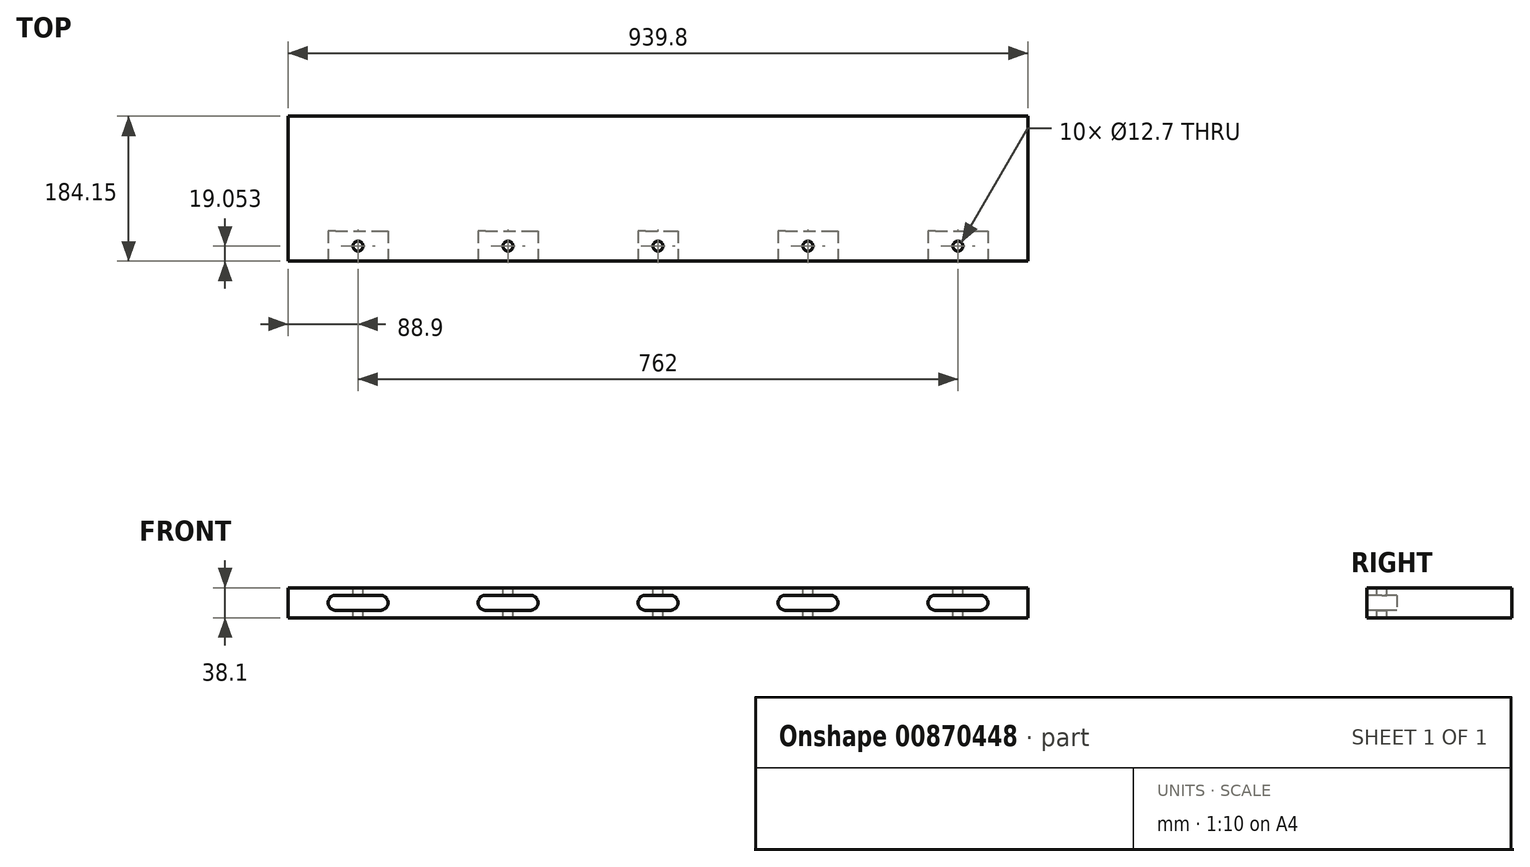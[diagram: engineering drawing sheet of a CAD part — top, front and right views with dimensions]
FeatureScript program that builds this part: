
annotation { "Feature Type Name" : "Feature", "Feature Type Description" : "" }
export const myFeature = defineFeature(function(context is Context, id is Id, definition is map)
    precondition{}
    {
        {
            var Q0;
            Q0=qCreatedBy(makeId("Right.planeOp"),FACE);
            var sketch = newSketch(context, id + "F0", { "sketchPlane" : qUnion([Q0])});
            skLineSegment(sketch, "E0.bottom", {"start": v(93.88, 19.05) * mm, "end": v(-90.27, 19.05) * mm});
            skLineSegment(sketch, "E0.top", {"start": v(93.88, -19.05) * mm, "end": v(-90.27, -19.05) * mm});
            skLineSegment(sketch, "E0.left", {"start": v(93.88, 19.05) * mm, "end": v(93.88, -19.05) * mm});
            skLineSegment(sketch, "E0.right", {"start": v(-90.27, 19.05) * mm, "end": v(-90.27, -19.05) * mm});
            skPoint(sketch, "E0.middle", {"position": v(1.8, 0) * mm});
            skSolve(sketch);
        }
        {
            var Q0;
            Q0=makeQuery(id+"F0.imprint","IMPRINT",FACE,{"disambiguationData":[TD([[makeQuery(id+"F0.imprint","IMPRINT",EDGE,{"derivedFrom":sQuery(id+"F0.wireOp",EDGE,"E0.bottom")}),1.0]])]});
            extrude(context, id + "F1", {"entities" : qUnion([Q0]), "depth" : 939.8 * mm, "offsetDistance" : 25.4 * mm});
        }
        {
            var Q0;
            Q0=makeQuery(id+"F1.opExtrude","SWEPT_FACE",FACE,{"disambiguationData":[OSD([sQuery(id+"F0.wireOp",EDGE,"E0.right")])]});
            var sketch = newSketch(context, id + "F2", { "sketchPlane" : qUnion([Q0])});
            skLineSegment(sketch, "E1.bottom", {"start": v(60.33, 9.53) * mm, "end": v(117.47, 9.53) * mm});
            skLineSegment(sketch, "E1.top", {"start": v(60.33, -9.52) * mm, "end": v(117.47, -9.52) * mm});
            skArc(sketch, "E2", {"start": v(60.33, 9.53) * mm, "mid": v(50.8, 0) * mm, "end": v(60.33, -9.53) * mm});
            skArc(sketch, "E3", {"start": v(117.47, 9.53) * mm, "mid": v(127, 0) * mm, "end": v(117.47, -9.53) * mm});
            skLineSegment(sketch, "E4", {"start": v(822.33, 9.53) * mm, "end": v(879.47, 9.53) * mm});
            skLineSegment(sketch, "E5", {"start": v(822.33, -9.53) * mm, "end": v(879.47, -9.53) * mm});
            skArc(sketch, "E6", {"start": v(822.33, 9.52) * mm, "mid": v(812.8, 0) * mm, "end": v(822.33, -9.52) * mm});
            skArc(sketch, "E7", {"start": v(879.47, 9.53) * mm, "mid": v(889, 0) * mm, "end": v(879.47, -9.53) * mm});
            skArc(sketch, "E8.1.0.0", {"start": v(250.83, 9.53) * mm, "mid": v(241.3, 0) * mm, "end": v(250.83, -9.53) * mm});
            skLineSegment(sketch, "E8.1.0.1", {"start": v(250.83, -9.52) * mm, "end": v(307.97, -9.52) * mm});
            skArc(sketch, "E8.1.0.2", {"start": v(307.97, 9.53) * mm, "mid": v(317.5, 0) * mm, "end": v(307.97, -9.53) * mm});
            skLineSegment(sketch, "E8.1.0.3", {"start": v(250.83, 9.53) * mm, "end": v(307.97, 9.53) * mm});
            skArc(sketch, "E8.2.0.0", {"start": v(441.33, 9.53) * mm, "mid": v(431.8, 0) * mm, "end": v(441.33, -9.53) * mm});
            skLineSegment(sketch, "E8.2.0.1", {"start": v(441.33, -9.52) * mm, "end": v(498.48, -9.52) * mm});
            skArc(sketch, "E8.2.0.2", {"start": v(498.48, 9.53) * mm, "mid": v(508, 0) * mm, "end": v(498.48, -9.53) * mm});
            skLineSegment(sketch, "E8.2.0.3", {"start": v(441.33, 9.53) * mm, "end": v(498.48, 9.53) * mm});
            skArc(sketch, "E8.3.0.0", {"start": v(631.83, 9.53) * mm, "mid": v(622.3, 0) * mm, "end": v(631.83, -9.53) * mm});
            skLineSegment(sketch, "E8.3.0.1", {"start": v(631.83, -9.52) * mm, "end": v(688.98, -9.52) * mm});
            skArc(sketch, "E8.3.0.2", {"start": v(688.98, 9.53) * mm, "mid": v(698.5, 0) * mm, "end": v(688.98, -9.53) * mm});
            skLineSegment(sketch, "E8.3.0.3", {"start": v(631.83, 9.53) * mm, "end": v(688.98, 9.53) * mm});
            skLineSegment(sketch, "E8.direction1", {"start": v(60.33, -9.53) * mm, "end": v(250.83, -9.53) * mm, "construction": true});
            skArc(sketch, "E9", {"start": v(454.03, 9.53) * mm, "mid": v(444.5, 0) * mm, "end": v(454.03, -9.53) * mm});
            skArc(sketch, "E10", {"start": v(485.78, -9.53) * mm, "mid": v(495.3, 0) * mm, "end": v(485.78, 9.53) * mm});
            skLineSegment(sketch, "E11", {"start": v(469.9, 23.51) * mm, "end": v(469.9, -33.12) * mm, "construction": true});
            skSolve(sketch);
        }
        {
            var Q0;
            Q0=makeQuery(id+"F2.imprint","IMPRINT",FACE,{"disambiguationData":[TD([[makeQuery(id+"F2.imprint","IMPRINT",EDGE,{"derivedFrom":sQuery(id+"F2.wireOp",EDGE,"E1.bottom")}),-1.0]])]});
            var Q1;
            Q1=makeQuery(id+"F2.imprint","IMPRINT",FACE,{"disambiguationData":[TD([[makeQuery(id+"F2.imprint","IMPRINT",EDGE,{"derivedFrom":sQuery(id+"F2.wireOp",EDGE,"E8.1.0.0")}),1.0]])]});
            var Q2;
            Q2=makeQuery(id+"F2.imprint","IMPRINT",FACE,{"disambiguationData":[TD([[makeQuery(id+"F2.imprint","IMPRINT",EDGE,{"derivedFrom":sQuery(id+"F2.wireOp",EDGE,"E8.3.0.0")}),1.0]])]});
            var Q3;
            Q3=makeQuery(id+"F2.imprint","IMPRINT",FACE,{"disambiguationData":[TD([[makeQuery(id+"F2.imprint","IMPRINT",EDGE,{"derivedFrom":sQuery(id+"F2.wireOp",EDGE,"E4")}),-1.0]])]});
            var Q4;
            {var subQ0=sQuery(id+"F2.wireOp",EDGE,"E9");Q4=makeQuery(id+"F2.imprint","IMPRINT",FACE,{"disambiguationData":[TD([[makeQuery(id+"F2.imprint","IMPRINT",EDGE,{"derivedFrom":subQ0}),1.0]])]});}
            extrude(context, id + "F3", {"entities" : qUnion([Q0, Q1, Q2, Q3, Q4]), "operationType" : NewBodyOperationType.REMOVE, "oppositeDirection" : true, "depth" : 38.1 * mm, "offsetDistance" : 25.4 * mm});
        }
        {
            var Q0;
            Q0=makeQuery(id+"F1.opExtrude","SWEPT_FACE",FACE,{"disambiguationData":[OSD([sQuery(id+"F0.wireOp",EDGE,"E0.bottom")])]});
            var sketch = newSketch(context, id + "F4", { "sketchPlane" : qUnion([Q0])});
            skCircle(sketch, "E12", {"center": v(88.9, -71.22) * mm, "radius": 6.35 * mm});
            skCircle(sketch, "E13", {"center": v(279.4, -71.22) * mm, "radius": 6.35 * mm});
            skCircle(sketch, "E14.1.0.0", {"center": v(469.9, -71.22) * mm, "radius": 6.35 * mm});
            skCircle(sketch, "E14.2.0.0", {"center": v(660.4, -71.22) * mm, "radius": 6.35 * mm});
            skCircle(sketch, "E14.3.0.0", {"center": v(850.9, -71.22) * mm, "radius": 6.35 * mm});
            skLineSegment(sketch, "E14.direction1", {"start": v(279.4, -71.22) * mm, "end": v(469.9, -71.22) * mm, "construction": true});
            skSolve(sketch);
        }
        {
            var Q0;
            Q0=makeQuery(id+"F4.imprint","IMPRINT",FACE,{"disambiguationData":[TD([[makeQuery(id+"F4.imprint","IMPRINT",EDGE,{"derivedFrom":sQuery(id+"F4.wireOp",EDGE,"E12")}),1.0]])]});
            var Q1;
            Q1=makeQuery(id+"F4.imprint","IMPRINT",FACE,{"disambiguationData":[TD([[makeQuery(id+"F4.imprint","IMPRINT",EDGE,{"derivedFrom":sQuery(id+"F4.wireOp",EDGE,"E13")}),1.0]])]});
            var Q2;
            Q2=makeQuery(id+"F4.imprint","IMPRINT",FACE,{"disambiguationData":[TD([[makeQuery(id+"F4.imprint","IMPRINT",EDGE,{"derivedFrom":sQuery(id+"F4.wireOp",EDGE,"E14.1.0.0")}),1.0]])]});
            var Q3;
            Q3=makeQuery(id+"F4.imprint","IMPRINT",FACE,{"disambiguationData":[TD([[makeQuery(id+"F4.imprint","IMPRINT",EDGE,{"derivedFrom":sQuery(id+"F4.wireOp",EDGE,"E14.2.0.0")}),1.0]])]});
            var Q4;
            Q4=makeQuery(id+"F4.imprint","IMPRINT",FACE,{"disambiguationData":[TD([[makeQuery(id+"F4.imprint","IMPRINT",EDGE,{"derivedFrom":sQuery(id+"F4.wireOp",EDGE,"E14.3.0.0")}),1.0]])]});
            var Q5;
            Q5=makeQuery(id+"F4.imprint","IMPRINT",FACE,{"disambiguationData":[TD([[makeQuery(id+"F4.imprint","IMPRINT",EDGE,{"derivedFrom":sQuery(id+"F4.wireOp",EDGE,"KxOhdoyV-Ap0P-3e35-0boH-RHxZr1wnbg2V")}),1.0]])]});
            extrude(context, id + "F5", {"entities" : qUnion([Q0, Q1, Q2, Q3, Q4, Q5]), "operationType" : NewBodyOperationType.REMOVE, "endBound" : BoundingType.THROUGH_ALL, "oppositeDirection" : true, "depth" : 25.4 * mm, "offsetDistance" : 25.4 * mm});
        }
    });
